# Revit family: S-659
name_source: partatom
category: Plumbing Fixtures
revit_build: Autodesk Revit 2015 (Build: 20140606_1530(x64)
units: mm (PartAtom-declared; Revit-internal decimal feet)

## types (4) — shared parameters
Description = SHOWER CHANNEL FOR TILED SHOWERS, REMOVABLE TRAP, ORIENTABLE HORIZONTAL OUTLET, WITH GRID SOFT, WITH HEIGHT REGULATION FEET
Emax = 16 mm  [stored 0.0524934 ft]
Emin = 6 mm  [stored 0.019685 ft]
Flowrate = 0.8 L/s
Grid = INOX AISI304
H_Diameter = 50 mm  [stored 0.164042 ft]
Hidraulic seal = 30 mm
Manufacturer = Jimten
Material = ABS
Model = S-659
Outlet = 40H/50M
Total Minimum Height = 75-85 mm
Type Comments = WITH PRESSING RING FOR WATERPROOFING PVC OR GEOTEXTILE MEMBRANES. WITH PROTECTION COVER.  WITH GRID HEIGHT ADJUSTABLE.
URL = http://www.jimten.com
WFU = 1

## per-type parameters (varying)
| type | A_Outlet | B_Grid | DistLegs | Reference | Size | Type Grid |
| 50x650mm_Soft | 689 mm  [stored 2.2605 ft] | 670 mm  [stored 2.19816 ft] | 500 mm  [stored 1.64042 ft] | 13446 | 650mm x 50mm | 11 |
| 50x750mm_Soft | 789 mm  [stored 2.58858 ft] | 770 mm  [stored 2.52625 ft] | 600 mm | 13447 | 750mm x 50mm | 12 |
| 50x850mm_Soft | 889 mm  [stored 2.91667 ft] | 870 mm  [stored 2.85433 ft] | 700 mm  [stored 2.29659 ft] | 13448 | 850mm x 50mm | 13 |
| 50x950mm_Soft | 989 mm  [stored 3.24475 ft] | 970 mm  [stored 3.18241 ft] | 800 mm  [stored 2.62467 ft] | 13449 | 950mm x 50mm | 14 |

note: [stored X ft] marks values corroborated as IEEE doubles in the binary element streams (Revit-internal decimal feet)

## geometry (parser evidence)
native form markers: Blend x3, Sweep x8
no freeform markers — native parametric forms only
